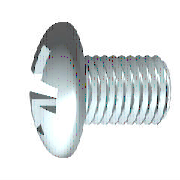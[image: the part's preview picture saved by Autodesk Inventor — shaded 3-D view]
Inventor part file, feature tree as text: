
AUTODESK INVENTOR PART (.ipt)
format: ipt  version: 2020 (Build 240168000, 168)  size: 271,872 bytes
history: native  units: mm (DEFAULTED — no unit token found)
features: extrude x1, other x1, plane x1
ambient origin geometry x7: Origin, YZ Plane, XZ Plane, X Axis, Y Axis, Z Axis, Center Point
bodies: Solid1 (feature_tree), Body (feature_tree)
feature tree (3):
  extrude  "Slot"  Depth=2.0mm
  other  "Cut"
  plane  "Work Plane3"
